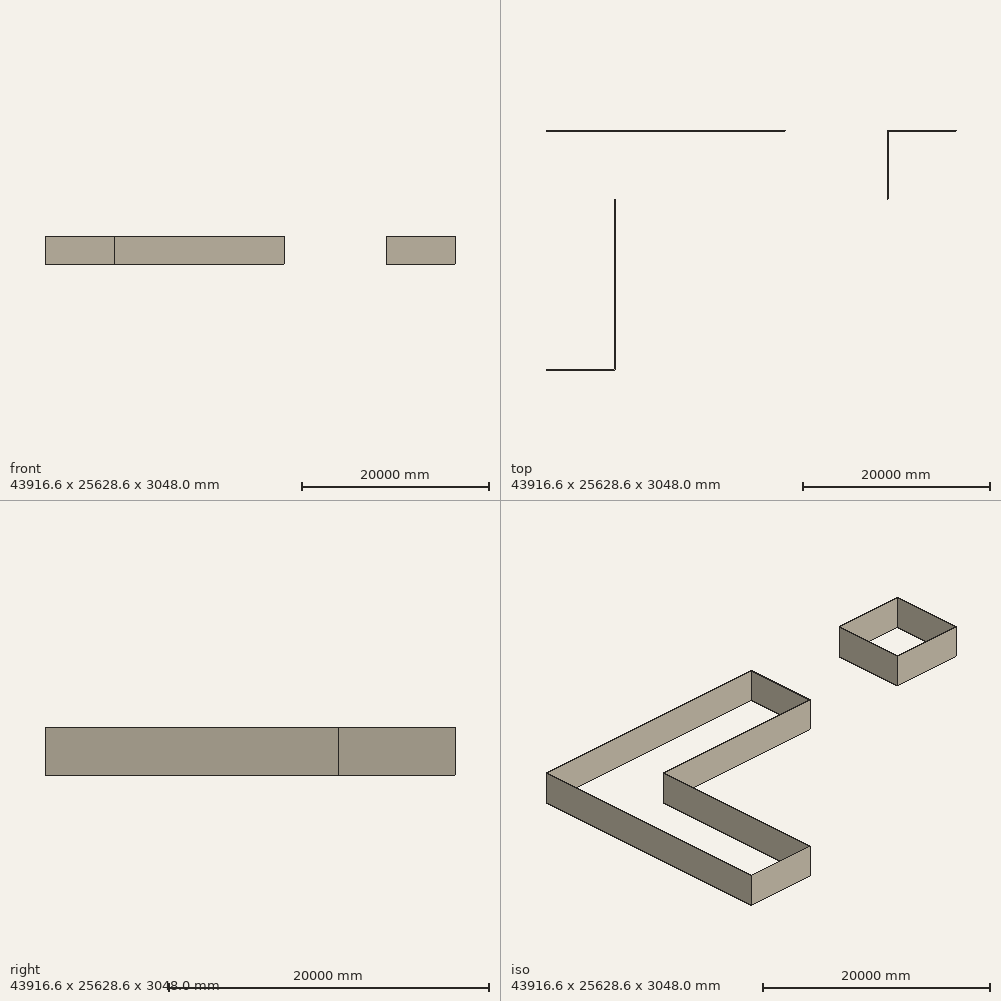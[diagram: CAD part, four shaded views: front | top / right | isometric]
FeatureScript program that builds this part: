
annotation { "Feature Type Name" : "Feature", "Feature Type Description" : "" }
export const myFeature = defineFeature(function(context is Context, id is Id, definition is map)
    precondition{}
    {
        {
            var Q0;
            Q0=qCreatedBy(makeId("Top.planeOp"),FACE);
            var sketch = newSketch(context, id + "F0", { "sketchPlane" : qUnion([Q0])});
            skLineSegment(sketch, "E0", {"start": v(914.4, -914.4) * mm, "end": v(26517.6, -914.4) * mm, "construction": true});
            skLineSegment(sketch, "E1", {"start": v(26517.6, -914.4) * mm, "end": v(26517.6, -8229.6) * mm, "construction": true});
            skLineSegment(sketch, "E2", {"start": v(26517.6, -8229.6) * mm, "end": v(8229.6, -8229.6) * mm, "construction": true});
            skLineSegment(sketch, "E3", {"start": v(8229.6, -8229.6) * mm, "end": v(8229.6, -26517.6) * mm, "construction": true});
            skLineSegment(sketch, "E4", {"start": v(8229.6, -26517.6) * mm, "end": v(914.4, -26517.6) * mm, "construction": true});
            skLineSegment(sketch, "E5", {"start": v(914.4, -26517.6) * mm, "end": v(914.4, -914.4) * mm, "construction": true});
            skLineSegment(sketch, "E6.bottom", {"start": v(37490.4, -914.4) * mm, "end": v(44805.6, -914.4) * mm, "construction": true});
            skLineSegment(sketch, "E6.top", {"start": v(37490.4, -8229.6) * mm, "end": v(44805.6, -8229.6) * mm, "construction": true});
            skLineSegment(sketch, "E6.left", {"start": v(37490.4, -914.4) * mm, "end": v(37490.4, -8229.6) * mm, "construction": true});
            skLineSegment(sketch, "E6.right", {"start": v(44805.6, -914.4) * mm, "end": v(44805.6, -8229.6) * mm, "construction": true});
            skLineSegment(sketch, "E7.0", {"start": v(927.1, -26504.9) * mm, "end": v(927.1, -927.1) * mm});
            skLineSegment(sketch, "E7.1", {"start": v(26504.9, -927.1) * mm, "end": v(26504.9, -8216.9) * mm});
            skLineSegment(sketch, "E7.2", {"start": v(26504.9, -8216.9) * mm, "end": v(8216.9, -8216.9) * mm});
            skLineSegment(sketch, "E7.3", {"start": v(927.1, -927.1) * mm, "end": v(26504.9, -927.1) * mm});
            skLineSegment(sketch, "E7.4", {"start": v(8216.9, -8216.9) * mm, "end": v(8216.9, -26504.9) * mm});
            skLineSegment(sketch, "E7.5", {"start": v(8216.9, -26504.9) * mm, "end": v(927.1, -26504.9) * mm});
            skLineSegment(sketch, "E8.0", {"start": v(901.7, -26530.3) * mm, "end": v(901.7, -901.7) * mm});
            skLineSegment(sketch, "E8.1", {"start": v(26530.3, -901.7) * mm, "end": v(26530.3, -8242.3) * mm});
            skLineSegment(sketch, "E8.2", {"start": v(26530.3, -8242.3) * mm, "end": v(8242.3, -8242.3) * mm});
            skLineSegment(sketch, "E8.3", {"start": v(901.7, -901.7) * mm, "end": v(26530.3, -901.7) * mm});
            skLineSegment(sketch, "E8.4", {"start": v(8242.3, -8242.3) * mm, "end": v(8242.3, -26530.3) * mm});
            skLineSegment(sketch, "E8.5", {"start": v(8242.3, -26530.3) * mm, "end": v(901.7, -26530.3) * mm});
            skLineSegment(sketch, "E9.0", {"start": v(37503.1, -927.1) * mm, "end": v(37503.1, -8216.9) * mm});
            skLineSegment(sketch, "E9.1", {"start": v(37503.1, -927.1) * mm, "end": v(44792.9, -927.1) * mm});
            skLineSegment(sketch, "E9.2", {"start": v(44792.9, -927.1) * mm, "end": v(44792.9, -8216.9) * mm});
            skLineSegment(sketch, "E9.3", {"start": v(37503.1, -8216.9) * mm, "end": v(44792.9, -8216.9) * mm});
            skLineSegment(sketch, "E10.0", {"start": v(37477.7, -901.7) * mm, "end": v(37477.7, -8242.3) * mm});
            skLineSegment(sketch, "E10.1", {"start": v(37477.7, -901.7) * mm, "end": v(44818.3, -901.7) * mm});
            skLineSegment(sketch, "E10.2", {"start": v(44818.3, -901.7) * mm, "end": v(44818.3, -8242.3) * mm});
            skLineSegment(sketch, "E10.3", {"start": v(37477.7, -8242.3) * mm, "end": v(44818.3, -8242.3) * mm});
            skSolve(sketch);
        }
        {
            var Q0;
            Q0=makeQuery(id+"F0.imprint","IMPRINT",FACE,{"disambiguationData":[TD([[makeQuery(id+"F0.imprint","IMPRINT",EDGE,{"derivedFrom":sQuery(id+"F0.wireOp",EDGE,"E7.0")}),1.0]])]});
            var Q1;
            Q1=makeQuery(id+"F0.imprint","IMPRINT",FACE,{"disambiguationData":[TD([[makeQuery(id+"F0.imprint","IMPRINT",EDGE,{"derivedFrom":sQuery(id+"F0.wireOp",EDGE,"E9.0")}),-1.0]])]});
            extrude(context, id + "F1", {"entities" : qUnion([Q0, Q1]), "depth" : 3048 * mm, "offsetDistance" : 30.48 * mm});
        }
    });
